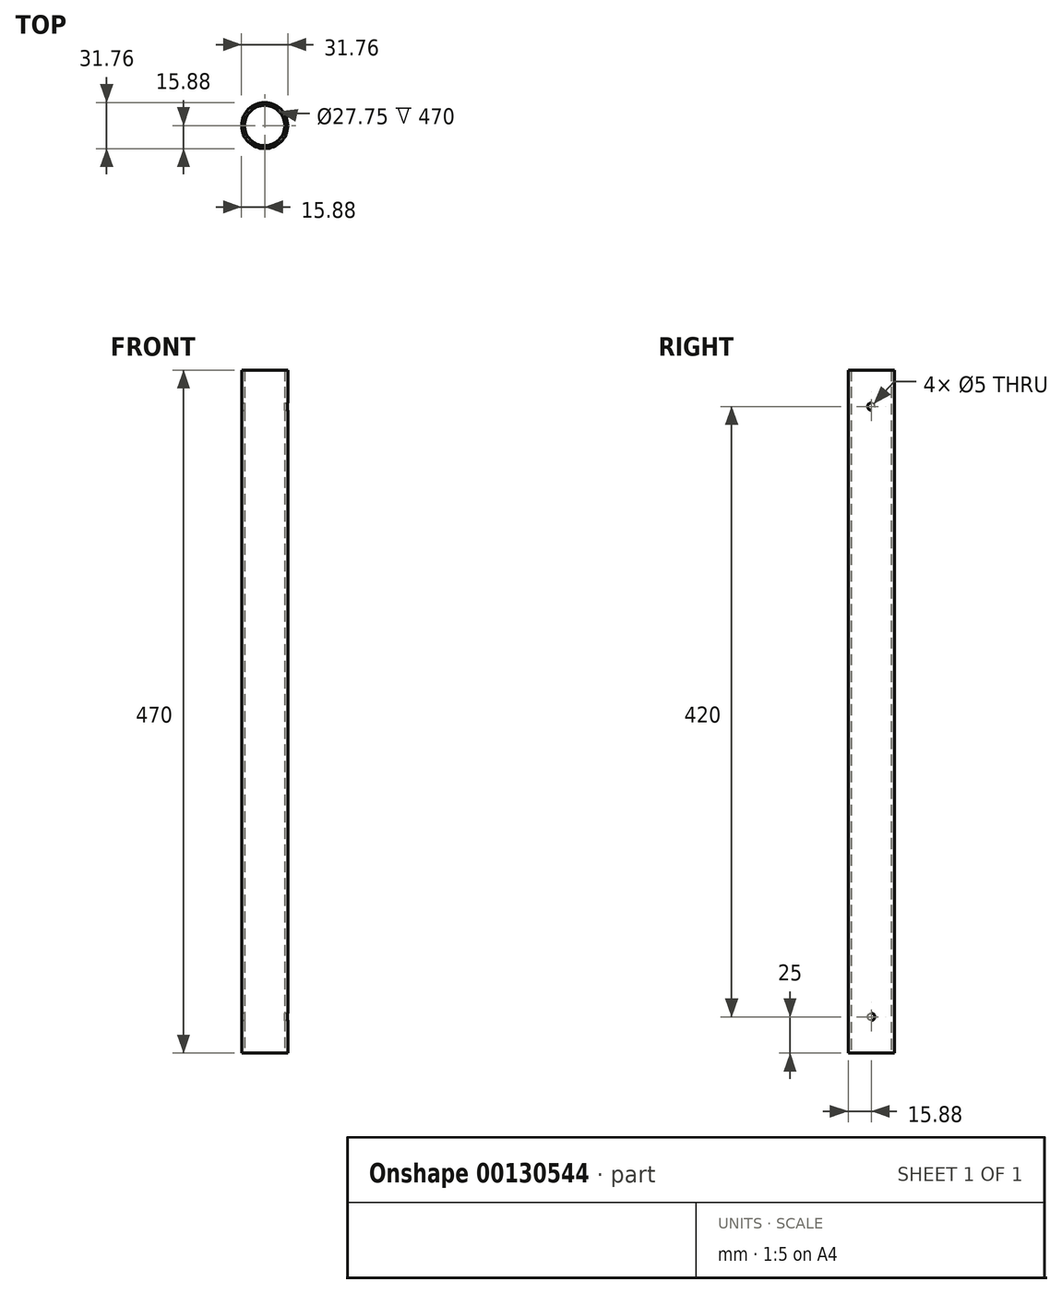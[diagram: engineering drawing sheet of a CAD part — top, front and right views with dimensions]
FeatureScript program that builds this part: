
annotation { "Feature Type Name" : "Feature", "Feature Type Description" : "" }
export const myFeature = defineFeature(function(context is Context, id is Id, definition is map)
    precondition{}
    {
        {
            var Q0;
            Q0=qCreatedBy(makeId("Top.planeOp"),FACE);
            var sketch = newSketch(context, id + "F0", { "sketchPlane" : qUnion([Q0])});
            skCircle(sketch, "E0", {"center": v(0, 0) * mm, "radius": 15.88 * mm});
            skCircle(sketch, "E1.0", {"center": v(0, 0) * mm, "radius": 13.88 * mm});
            skSolve(sketch);
        }
        {
            var Q0;
            Q0=makeQuery(id+"F0.imprint","IMPRINT",FACE,{"disambiguationData":[TD([[makeQuery(id+"F0.imprint","IMPRINT",EDGE,{"derivedFrom":sQuery(id+"F0.wireOp",EDGE,"E0")}),1.0]])]});
            extrude(context, id + "F1", {"entities" : qUnion([Q0]), "depth" : 470 * mm});
        }
        {
            var Q0;
            Q0=qCreatedBy(makeId("Right.planeOp"),FACE);
            var sketch = newSketch(context, id + "F2", { "sketchPlane" : qUnion([Q0])});
            skCircle(sketch, "E2", {"center": v(0, 25) * mm, "radius": 2.5 * mm});
            skSolve(sketch);
        }
        {
            var Q0;
            Q0 = qSketchRegion(id + "F2", true);
            extrude(context, id + "F3", {"entities" : qUnion([Q0]), "operationType" : NewBodyOperationType.REMOVE, "depth" : 30 * mm, "hasSecondDirection" : true, "secondDirectionOppositeDirection" : true, "secondDirectionDepth" : 30 * mm});
        }
        {
            var Q0;
            Q0=qCreatedBy(makeId("Right.planeOp"),FACE);
            var sketch = newSketch(context, id + "F4", { "sketchPlane" : qUnion([Q0])});
            skCircle(sketch, "E3", {"center": v(0, 445) * mm, "radius": 2.5 * mm});
            skSolve(sketch);
        }
        {
            var Q0;
            Q0 = qSketchRegion(id + "F4", true);
            extrude(context, id + "F5", {"entities" : qUnion([Q0]), "operationType" : NewBodyOperationType.REMOVE, "oppositeDirection" : true, "depth" : 25 * mm, "hasSecondDirection" : true, "secondDirectionOppositeDirection" : false, "secondDirectionDepth" : 25 * mm});
        }
    });
